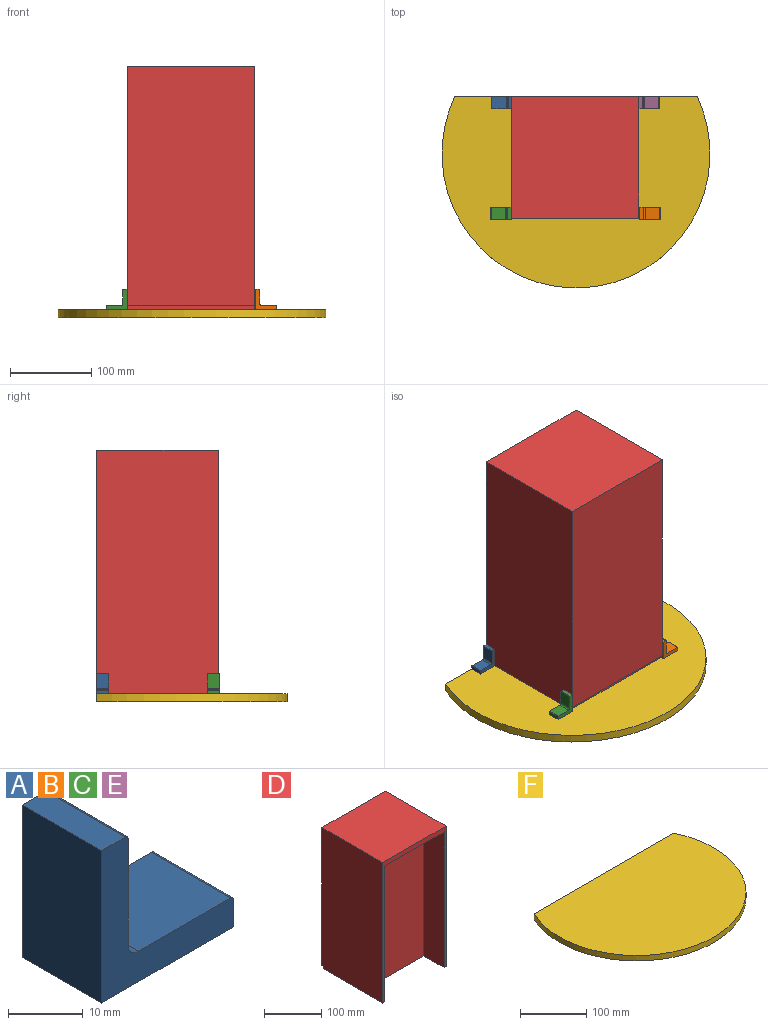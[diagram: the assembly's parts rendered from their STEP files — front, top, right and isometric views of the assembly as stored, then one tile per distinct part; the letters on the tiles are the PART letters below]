
ASSEMBLY  parts=6 mates=3
PART A: 11 faces, bbox 25x15x25 mm
  f0: plane 15x4.5mm, normal (0,0,1), area 67.5mm2, adj f1,f6,f7,f10
  f1: plane 25x15mm, normal (-1,0,0), area 375mm2, adj f0,f2,f6,f7
  f2: plane 25x15mm, normal (0,0,-1), area 375mm2, adj f1,f3,f6,f7
  f3: plane 15x4.5mm, normal (1,0,0), area 67.5mm2, adj f2,f6,f7,f9
  f4: plane 17.5x15mm, normal (0,0,1), area 262.5mm2, adj f6,f7,f8,f9
  f5: plane 17.5x15mm, normal (1,0,0), area 262.5mm2, adj f6,f7,f8,f10
  f6: plane 25x25mm, normal (0,-1,0), area 225.8mm2, adj f0,f1,f2,f3,f4,f5,f8,f9
  f7: plane 25x25mm, normal (0,1,0), area 225.8mm2, adj f0,f1,f2,f3,f4,f5,f8,f9
  f8: cylinder r=2mm len=15mm, axis (0,-1,0), area 47.1mm2, adj f4,f5,f6,f7
  f9: cylinder r=0.5mm len=15mm, axis (0,1,0), area 11.8mm2, adj f3,f4,f6,f7
  f10: cylinder r=0.5mm len=15mm, axis (0,1,0), area 11.8mm2, adj f0,f5,f6,f7
PART B: same geometry as A
PART C: same geometry as A
PART D: 12 faces, bbox 156.5x150x300 mm
  f0: plane 300x150mm, normal (-1,0,0), area 44985mm2, adj f1,f2,f4,f5,f10,f11
  f1: plane 156.5x147mm, normal (0,0,-1), area 15680.5mm2, adj f0,f2,f3,f6,f8,f9,f11
  f2: plane 300x156.5mm, normal (0,-1,0), area 4465mm2, adj f0,f1,f3,f5,f6,f7,f8
  f3: plane 300x150mm, normal (1,0,0), area 44985mm2, adj f1,f2,f4,f5,f10,f11
  f4: plane 295x156.5mm, normal (0,1,0), area 46167.5mm2, adj f0,f3,f5,f10
  f5: plane 156.5x150mm, normal (0,0,1), area 23475mm2, adj f0,f2,f3,f4
  f6: plane 290x50mm, normal (-1,0,0), area 14500mm2, adj f1,f2,f7,f9
  f7: plane 146.5x50mm, normal (0,0,-1), area 7325mm2, adj f2,f6,f8,f9
  f8: plane 290x50mm, normal (1,0,0), area 14500mm2, adj f1,f2,f7,f9
  f9: plane 290x146.5mm, normal (0,-1,0), area 42485mm2, adj f1,f6,f7,f8
  f10: plane 156.5x3mm, normal (0,0,-1), area 469.5mm2, adj f0,f3,f4,f11
  f11: plane 156.5x5mm, normal (0,1,0), area 782.5mm2, adj f0,f1,f3,f10
PART E: same geometry as A
PART F: 4 faces, bbox 330x235.4x10 mm
  f0: cylinder r=165mm len=330mm, axis (0,0,-1), area 6637.2mm2, adj f1,f2,f3
  f1: plane 298.5x10mm, normal (0,1,0), area 2985mm2, adj f0,f2,f3
  f2: plane 330x235.35mm, normal (0,0,1), area 65257.2mm2, adj f0,f1
  f3: plane 330x235.35mm, normal (0,0,-1), area 65257.2mm2, adj f0,f1
PLACE A rot(axis=(0,0,-1),180deg) t=(512.57,52.23,-93.83)mm
PLACE B t=(670.07,-68.77,-93.83)mm
PLACE C rot(axis=(0,0,-1),180deg) t=(511.57,-83.77,-93.83)mm
PLACE D rot(axis=(0,0,-1),180deg) t=(590.82,-7.77,-93.83)mm
PLACE E t=(669.07,67.23,-93.83)mm
PLACE F rot(axis=(-0.07,0.43,0.9),0deg) t=(591.57,-8.77,-103.83)mm
MATE fastened E.f1 <-> D.f0  axis (-1,0,0) through (669.07,67.23,-93.83)mm
MATE fastened D.f2 <-> F.f1  axis (0,1,0) through (517.57,67.23,-93.83)mm
MATE fastened A.f1 <-> D.f3  axis (1,0,0) through (512.57,67.23,-93.83)mm
